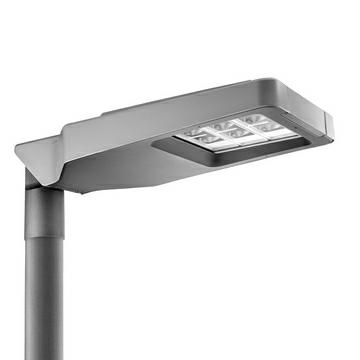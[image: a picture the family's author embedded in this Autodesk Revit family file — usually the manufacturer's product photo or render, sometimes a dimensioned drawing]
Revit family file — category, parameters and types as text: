
# Revit family: Lighting-Stradale-GEWISS-ROAD[5]MINI-LED_OTTICA_HUGE_CLI
name_source: partatom
category: Apparecchi per illuminazione
units: mm (PartAtom-declared; Revit-internal decimal feet)

## family parameters
Basato su piano di lavoro = No
Condiviso = No
Punto di calcolo locali = No
Quota connettore circolare = Usa diametro
Sempre verticale = Sì
Sorgente d'illuminazione = No
Taglio con vuoti quando caricato = No
Tipo di parte = Normale

## types (1)
- Lighting-Stradale-GEWISS-ROAD[5]MINI-LED_OTTICA_HUGE_CLI
    Alimentatore = Incluso
    Apparecchio a ridotta temperatura superficiale = -
    Applicazione = Esterno
    Cablaggio = Sezionatore
    Caratteristiche elettriche e gestione della luce = -
    Caratteristiche ottiche e illuminotecniche = -
    Carico apparente = 53 VA
    Catalogo = LIGHTING
    Catalogo Serie = ROAD [5]
    Certificazione DIN 18032-3 = -
    Certificazioni e classificazioni = -
    Classe fotobiologica = RG0
    Classe isolamento = I
    Classificazione: = -
    Codice Electrocod = 244C
    Codice digitale univoco (Datamatrix) = Attualmente non presente
    Colore = Grigio grafite
    Commenti sul wattaggio = 53W
    Contesto = Illuminazione stradale e parcheggi
    Controllo abbagliamento e luminanza = G*3 - ULOR = 0
    Corpo = Alluminio pressofuso
    Corrente di pilotaggio. = 0,7A
    Descrizione = GWR5672M30K - ROAD5 MINI HUGE 2M 3000K 0,7A CL1 1-10V
    Dispositivo di protezione = DM 10KV / CM 10KV
    Distanza minima dall'oggetto illuminato = 1M
    Durata di vita = L90B10 (Tq+25°C) = 100.000 h - L90B10 (Tq+50°C) = 75.000 h
    Efficienza luminosa (lm/W) = 96
    Finitura colore = Verniciato a polveri
    Fissaggio = Testa palo - Sbraccio
    Flusso nominale (lm) = 5400
    Frequenza nominale (Hz) = 50 / 60
    Funzionalità alimentatore = Dimmerabile
    Gancio di chiusura = Maniglia frontale integrata
    Garanzia = 5 anni
    Grado di protezione = IP66
    Gruppo ottico = Riflettore in PC metallizzato
    Guarnizioni = silicone antinvecchiamento
    IDF = 7c3ec403-921e-44eb-8bcd-a645f059971d
    IDT = 6eb1c969380f487eb4332d009c9c34aa
    IPEA = STRADALE = A++ // GRANDI AREE = A++ // CICLOPEDONALI = A+ // AREE VERDI = A+ // CENTRO STORICO = A5+
    Immagine tipo = GWR5276M.jpg
    Inclinazione = -20° ÷ +10° sbraccio - -10° ÷ +20° testa palo
    Indice di resa cromatica = CRI-70
    Informazioni generali = -
    Installazione e manutenzione = -
    LED Life Time (L80B05) = 77000H
    Lampada = LED
    Lampada: = LED
    Lumen output (lm) = 5200
    Materiali = -
    Modello = GWR5672M30K
    Norma di riferimento = EN 60598-2-3, EN 60598-1 IEC/TR 62778
    Numero moduli = 2 (2x3 LED)
    Ottica = HUGE
    Peso (kg): = 6,6
    Potenza assorbita : = 54 W @ 0.7A
    Potenza di sistema = 53W
    Produttore = GEWISS S.p.A.
    Regolazione inclinazione = -20° ÷ +10° sbraccio - -10° ÷ +20° testa palo
    Resistenza agli urti = IK08
    Resistenza al filo incandescente = -
    Resistenza alle sovratensioni : = 10 KV in modalità comune e differenziale
    SEO = Stradale
    Scheda Tecnica = https://www.gewiss.com
    Schermo = Vetro piano temperato spessore 4mm
    Sistema di controllo = Dimmerabile 1-10 V
    Sostituibilità gruppo ottico = Non disponibile
    Sostituibilità piastra di cablaggio = Non disponibile
    Superficie massima esposta al vento = 0,149999999999999M2
    Superficie massima esposta al vento : = 0,15 m²
    Temperatura di colore = 3000K
    Temperatura di colore: = 3000 K (CRI>80)
    Temperatura di esercizio = -25 +50 °C
    Temperatura di stoccaggio = -
    Temperatura di utilizzo = -25 +50 °C
    Tensione = 220/240 V - 50/60 Hz - Dimmerabile 1-10 V
    Tensione di alimentazione = 220 - 240 V
    Tipo alimentatore = Driver Led in corrente continua
    Tipo di apparecchio = Apparecchiatura stradale a LED
    Tipo di installazione e montaggio = Testa palo - Sbraccio
    Tipologia = Dimmerabile
    Tipologia sorgente luminosa = LED - Non sostituibile
    Tolleranza cromatica = SDCM = 5
    URL = https://www.gewiss.com
    Vano di alimentazione = Integrato
    Versione file RFA = 20.11
    Viti esterne = Acciaio inox
